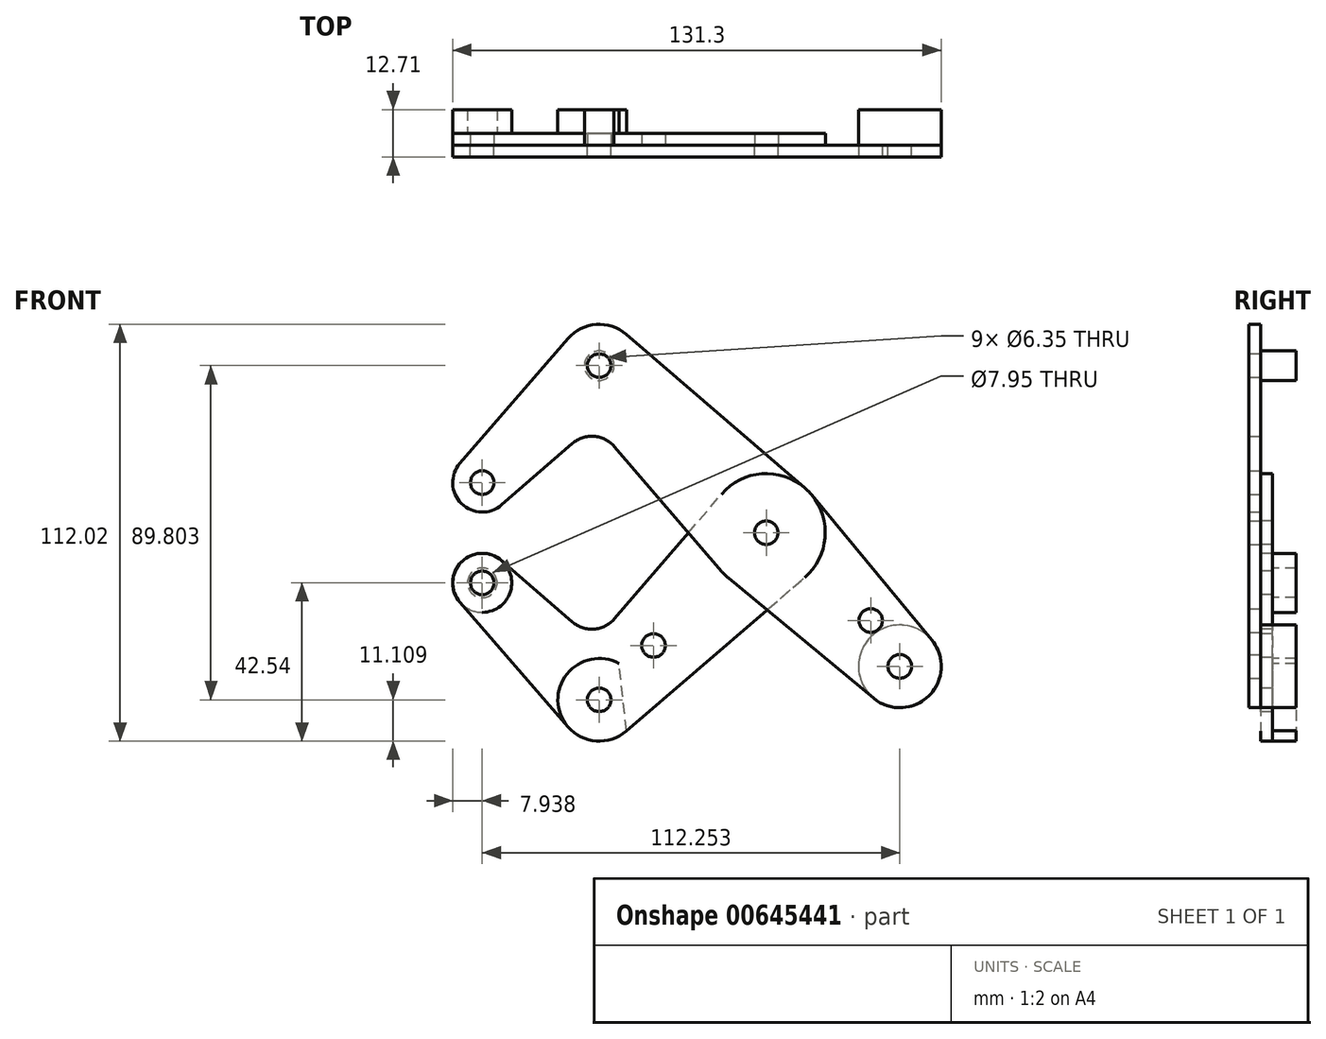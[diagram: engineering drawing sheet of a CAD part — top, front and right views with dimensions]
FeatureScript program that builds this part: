
annotation { "Feature Type Name" : "Feature", "Feature Type Description" : "" }
export const myFeature = defineFeature(function(context is Context, id is Id, definition is map)
    precondition{}
    {
        {
            var Q0;
            Q0=qCreatedBy(makeId("Front.planeOp"),FACE);
            var sketch = newSketch(context, id + "F0", { "sketchPlane" : qUnion([Q0])});
            skLineSegment(sketch, "E0", {"start": v(-76.33, 13.47) * mm, "end": v(-44.9, 44.9) * mm, "construction": true});
            skLineSegment(sketch, "E1", {"start": v(-44.9, 44.9) * mm, "end": v(35.92, -35.92) * mm, "construction": true});
            skCircle(sketch, "E2", {"center": v(-76.33, 13.47) * mm, "radius": 7.94 * mm});
            skCircle(sketch, "E3", {"center": v(-44.9, 44.9) * mm, "radius": 3.18 * mm});
            skCircle(sketch, "E4", {"center": v(-44.9, 44.9) * mm, "radius": 11.11 * mm});
            skCircle(sketch, "E5", {"center": v(0, 0) * mm, "radius": 15.88 * mm});
            skCircle(sketch, "E6", {"center": v(0, 0) * mm, "radius": 3.98 * mm});
            skCircle(sketch, "E7", {"center": v(35.92, -35.92) * mm, "radius": 11.11 * mm});
            skCircle(sketch, "E8", {"center": v(35.92, -35.92) * mm, "radius": 3.18 * mm});
            skCircle(sketch, "E9", {"center": v(-76.33, 13.47) * mm, "radius": 3.18 * mm});
            skCircle(sketch, "E10", {"center": v(0, 0) * mm, "radius": 3.18 * mm});
            skCircle(sketch, "E11", {"center": v(28.07, -23.58) * mm, "radius": 3.18 * mm});
            skLineSegment(sketch, "E12", {"start": v(-82.33, 18.67) * mm, "end": v(-53.3, 52.18) * mm});
            skLineSegment(sketch, "E13", {"start": v(-71.13, 7.47) * mm, "end": v(-52.08, 23.98) * mm});
            skLineSegment(sketch, "E14", {"start": v(-40.85, 23.15) * mm, "end": v(-12.04, -10.35) * mm});
            skLineSegment(sketch, "E15", {"start": v(-10.12, -12.23) * mm, "end": v(28.83, -44.48) * mm});
            skLineSegment(sketch, "E16", {"start": v(-37.66, 53.33) * mm, "end": v(10.35, 12.04) * mm});
            skLineSegment(sketch, "E17", {"start": v(12.23, 10.12) * mm, "end": v(44.48, -28.83) * mm});
            skLineSegment(sketch, "E18", {"start": v(0, 0) * mm, "end": v(11.23, 11.23) * mm, "construction": true});
            skArc(sketch, "E19.filletArc", {"start": v(-40.85, 23.15) * mm, "mid": v(-46.3, 25.9) * mm, "end": v(-52.08, 23.98) * mm});
            skLineSegment(sketch, "E20", {"start": v(0, 0) * mm, "end": v(-44.9, -44.9) * mm, "construction": true});
            skLineSegment(sketch, "E21", {"start": v(-44.9, -44.9) * mm, "end": v(-76.33, -13.47) * mm, "construction": true});
            skCircle(sketch, "E22", {"center": v(-76.33, -13.47) * mm, "radius": 7.94 * mm});
            skCircle(sketch, "E23", {"center": v(-76.33, -13.47) * mm, "radius": 3.18 * mm});
            skCircle(sketch, "E24", {"center": v(-44.9, -44.9) * mm, "radius": 11.11 * mm});
            skCircle(sketch, "E25", {"center": v(-30.3, -30.3) * mm, "radius": 3.18 * mm});
            skCircle(sketch, "E26", {"center": v(-44.9, -44.9) * mm, "radius": 3.18 * mm});
            skLineSegment(sketch, "E27", {"start": v(-82.33, -18.67) * mm, "end": v(-53.3, -52.18) * mm});
            skLineSegment(sketch, "E28", {"start": v(-71.13, -7.47) * mm, "end": v(-52.08, -23.98) * mm});
            skLineSegment(sketch, "E29", {"start": v(-40.85, -23.15) * mm, "end": v(-12.04, 10.35) * mm});
            skLineSegment(sketch, "E30", {"start": v(-37.66, -53.33) * mm, "end": v(10.35, -12.04) * mm});
            skArc(sketch, "E31.filletArc", {"start": v(-52.08, -23.98) * mm, "mid": v(-46.3, -25.9) * mm, "end": v(-40.85, -23.15) * mm});
            skSolve(sketch);
        }
        {
            var Q0;
            Q0=makeQuery(id+"F0.imprint","IMPRINT",FACE,{"disambiguationData":[TD([[makeQuery(id+"F0.imprint","IMPRINT",EDGE,{"derivedFrom":sQuery(id+"F0.wireOp",EDGE,"E9")}),-1.0]])]});
            var Q1;
            {var subQ0=sQuery(id+"F0.wireOp",EDGE,"E12");Q1=makeQuery(id+"F0.imprint","IMPRINT",FACE,{"disambiguationData":[TD([[makeQuery(id+"F0.imprint","IMPRINT",EDGE,{"derivedFrom":subQ0}),-1.0]])]});}
            var Q2;
            Q2=makeQuery(id+"F0.imprint","IMPRINT",FACE,{"disambiguationData":[TD([[makeQuery(id+"F0.imprint","IMPRINT",EDGE,{"derivedFrom":sQuery(id+"F0.wireOp",EDGE,"E3")}),-1.0]])]});
            var Q3;
            {var subQ0=sQuery(id+"F0.wireOp",EDGE,"E14");var subQ1=sQuery(id+"F0.wireOp",EDGE,"E5");var subQ2=makeQuery(id+"F0.imprint","INTERSECT",VERTEX,{"derivedFrom":[subQ1,subQ0]});Q3=makeQuery(id+"F0.imprint","IMPRINT",FACE,{"disambiguationData":[TD([[makeQuery(id+"F0.imprint","IMPRINT",EDGE,{"disambiguationData":[TD([[subQ2,1.0]])],"derivedFrom":subQ1}),-1.0]])]});}
            var Q4;
            Q4=makeQuery(id+"F0.imprint","IMPRINT",FACE,{"disambiguationData":[TD([[makeQuery(id+"F0.imprint","IMPRINT",EDGE,{"derivedFrom":sQuery(id+"F0.wireOp",EDGE,"E6")}),-1.0]])]});
            var Q5;
            Q5=makeQuery(id+"F0.imprint","IMPRINT",FACE,{"disambiguationData":[TD([[makeQuery(id+"F0.imprint","IMPRINT",EDGE,{"derivedFrom":sQuery(id+"F0.wireOp",EDGE,"E6")}),1.0]])]});
            var Q6;
            Q6=makeQuery(id+"F0.imprint","IMPRINT",FACE,{"disambiguationData":[TD([[makeQuery(id+"F0.imprint","IMPRINT",EDGE,{"derivedFrom":sQuery(id+"F0.wireOp",EDGE,"E11")}),-1.0]])]});
            var Q7;
            Q7=makeQuery(id+"F0.imprint","IMPRINT",FACE,{"disambiguationData":[TD([[makeQuery(id+"F0.imprint","IMPRINT",EDGE,{"derivedFrom":sQuery(id+"F0.wireOp",EDGE,"E8")}),-1.0]])]});
            var Q8;
            {var subQ0=sQuery(id+"F0.wireOp",EDGE,"E15");var subQ1=sQuery(id+"F0.wireOp",EDGE,"E5");var subQ2=makeQuery(id+"F0.imprint","INTERSECT",VERTEX,{"derivedFrom":[subQ1,subQ0]});Q8=makeQuery(id+"F0.imprint","IMPRINT",FACE,{"disambiguationData":[TD([[makeQuery(id+"F0.imprint","IMPRINT",EDGE,{"disambiguationData":[TD([[subQ2,-1.0]])],"derivedFrom":subQ1}),-1.0]])]});}
            extrude(context, id + "F1", {"entities" : qUnion([Q0, Q1, Q2, Q3, Q4, Q5, Q6, Q7, Q8]), "depth" : 3.17 * mm, "offsetDistance" : 25.4 * mm});
        }
        {
            var Q0;
            Q0=makeQuery(id+"F0.imprint","IMPRINT",FACE,{"disambiguationData":[TD([[makeQuery(id+"F0.imprint","IMPRINT",EDGE,{"derivedFrom":sQuery(id+"F0.wireOp",EDGE,"E23")}),-1.0]])]});
            var Q1;
            Q1=makeQuery(id+"F0.imprint","IMPRINT",FACE,{"disambiguationData":[TD([[makeQuery(id+"F0.imprint","IMPRINT",EDGE,{"derivedFrom":sQuery(id+"F0.wireOp",EDGE,"E25")}),-1.0]])]});
            var Q2;
            Q2=makeQuery(id+"F0.imprint","IMPRINT",FACE,{"disambiguationData":[TD([[makeQuery(id+"F0.imprint","IMPRINT",EDGE,{"derivedFrom":sQuery(id+"F0.wireOp",EDGE,"E26")}),-1.0]])]});
            var Q3;
            {var subQ0=sQuery(id+"F0.wireOp",EDGE,"E14");var subQ1=sQuery(id+"F0.wireOp",EDGE,"E5");var subQ2=makeQuery(id+"F0.imprint","INTERSECT",VERTEX,{"derivedFrom":[subQ1,subQ0]});Q3=makeQuery(id+"F0.imprint","IMPRINT",FACE,{"disambiguationData":[TD([[makeQuery(id+"F0.imprint","IMPRINT",EDGE,{"disambiguationData":[TD([[subQ2,1.0]])],"derivedFrom":subQ1}),-1.0]])]});}
            var Q4;
            {var subQ0=sQuery(id+"F0.wireOp",EDGE,"E15");var subQ1=sQuery(id+"F0.wireOp",EDGE,"E5");var subQ2=makeQuery(id+"F0.imprint","INTERSECT",VERTEX,{"derivedFrom":[subQ1,subQ0]});Q4=makeQuery(id+"F0.imprint","IMPRINT",FACE,{"disambiguationData":[TD([[makeQuery(id+"F0.imprint","IMPRINT",EDGE,{"disambiguationData":[TD([[subQ2,-1.0]])],"derivedFrom":subQ1}),-1.0]])]});}
            var Q5;
            Q5=makeQuery(id+"F0.imprint","IMPRINT",FACE,{"disambiguationData":[TD([[makeQuery(id+"F0.imprint","IMPRINT",EDGE,{"derivedFrom":sQuery(id+"F0.wireOp",EDGE,"E6")}),1.0]])]});
            var Q6;
            Q6=makeQuery(id+"F0.imprint","IMPRINT",FACE,{"disambiguationData":[TD([[makeQuery(id+"F0.imprint","IMPRINT",EDGE,{"derivedFrom":sQuery(id+"F0.wireOp",EDGE,"E6")}),-1.0]])]});
            var Q7;
            Q7=makeQuery(id+"F1.opExtrude","CAP_FACE",FACE,{"disambiguationData":[OSD([sQuery(id+"F0.wireOp",EDGE,"E2"),sQuery(id+"F0.wireOp",EDGE,"E3"),sQuery(id+"F0.wireOp",EDGE,"E4"),sQuery(id+"F0.wireOp",EDGE,"E5"),sQuery(id+"F0.wireOp",EDGE,"E7"),sQuery(id+"F0.wireOp",EDGE,"E8"),sQuery(id+"F0.wireOp",EDGE,"E9"),sQuery(id+"F0.wireOp",EDGE,"E10"),sQuery(id+"F0.wireOp",EDGE,"E11"),sQuery(id+"F0.wireOp",EDGE,"E12"),sQuery(id+"F0.wireOp",EDGE,"E13"),sQuery(id+"F0.wireOp",EDGE,"E14"),sQuery(id+"F0.wireOp",EDGE,"E15"),sQuery(id+"F0.wireOp",EDGE,"E16"),sQuery(id+"F0.wireOp",EDGE,"E17"),sQuery(id+"F0.wireOp",EDGE,"E19.filletArc"),sQuery(id+"F0.wireOp",EDGE,"E30")])],"isStart":false});
            extrude(context, id + "F2", {"entities" : qUnion([Q0, Q1, Q2, Q3, Q4, Q5, Q6, Q7]), "oppositeDirection" : true, "depth" : 3.17 * mm, "offsetDistance" : 25.4 * mm});
        }
        {
            var Q0;
            Q0=makeQuery(id+"F1.opExtrude","CAP_FACE",FACE,{"disambiguationData":[OSD([sQuery(id+"F0.wireOp",EDGE,"E2"),sQuery(id+"F0.wireOp",EDGE,"E3"),sQuery(id+"F0.wireOp",EDGE,"E4"),sQuery(id+"F0.wireOp",EDGE,"E5"),sQuery(id+"F0.wireOp",EDGE,"E7"),sQuery(id+"F0.wireOp",EDGE,"E8"),sQuery(id+"F0.wireOp",EDGE,"E9"),sQuery(id+"F0.wireOp",EDGE,"E10"),sQuery(id+"F0.wireOp",EDGE,"E11"),sQuery(id+"F0.wireOp",EDGE,"E12"),sQuery(id+"F0.wireOp",EDGE,"E13"),sQuery(id+"F0.wireOp",EDGE,"E14"),sQuery(id+"F0.wireOp",EDGE,"E15"),sQuery(id+"F0.wireOp",EDGE,"E16"),sQuery(id+"F0.wireOp",EDGE,"E17"),sQuery(id+"F0.wireOp",EDGE,"E19.filletArc")])],"isStart":false});
            var sketch = newSketch(context, id + "F3", { "sketchPlane" : qUnion([Q0])});
            skCircle(sketch, "E32", {"center": v(-44.9, 44.9) * mm, "radius": 3.98 * mm});
            skCircle(sketch, "E33.0", {"center": v(35.92, -35.92) * mm, "radius": 11.11 * mm});
            skSolve(sketch);
        }
        {
            var Q0;
            Q0=makeQuery(id+"F0.imprint","IMPRINT",FACE,{"disambiguationData":[TD([[makeQuery(id+"F0.imprint","IMPRINT",EDGE,{"derivedFrom":sQuery(id+"F0.wireOp",EDGE,"E25")}),-1.0]])]});
            var sketch = newSketch(context, id + "F4", { "sketchPlane" : qUnion([Q0])});
            skCircle(sketch, "E34.0", {"center": v(-76.33, -13.47) * mm, "radius": 7.94 * mm});
            skCircle(sketch, "E35", {"center": v(-76.33, -13.47) * mm, "radius": 3.98 * mm});
            skLineSegment(sketch, "E36.0", {"start": v(-71.13, -7.47) * mm, "end": v(-52.08, -23.98) * mm});
            skArc(sketch, "E37.0", {"start": v(-39.6, -35.14) * mm, "mid": v(-55.95, -46.13) * mm, "end": v(-37.58, -53.26) * mm});
            skLineSegment(sketch, "E38", {"start": v(-44.9, -44.9) * mm, "end": v(35.92, -35.92) * mm, "construction": true});
            skLineSegment(sketch, "E39", {"start": v(-39.6, -35.14) * mm, "end": v(-37.58, -53.26) * mm});
            skSolve(sketch);
        }
        {
            var Q0;
            Q0=qCreatedBy(makeId("Front.planeOp"),FACE);
            cPlane(context, id + "F5", {"entities" : qUnion([Q0]), "cplaneType" : CPlaneType.OFFSET, "offset" : 9.52 * mm, "oppositeDirection" : true, "width" : 152.4 * mm, "height" : 152.4 * mm});
        }
        {
            var Q0;
            Q0 = qSketchRegion(id + "F3", true);
            var Q1;
            Q1 = qSketchRegion(id + "F4", true);
            var Q2;
            Q2=qCreatedBy(id+"F5.planeOp",FACE);
            extrude(context, id + "F6", {"entities" : qUnion([Q0, Q1]), "endBound" : BoundingType.UP_TO_SURFACE, "oppositeDirection" : true, "depth" : 25.4 * mm, "endBoundEntityFace" : qUnion([Q2]), "offsetDistance" : 25.4 * mm});
        }
        {
            var Q0;
            Q0=makeQuery(id+"F2.opExtrude","SWEPT_BODY",BODY,{"disambiguationData":[OSD([sQuery(id+"F0.wireOp",EDGE,"E5"),sQuery(id+"F0.wireOp",EDGE,"E10"),sQuery(id+"F0.wireOp",EDGE,"E22"),sQuery(id+"F0.wireOp",EDGE,"E23"),sQuery(id+"F0.wireOp",EDGE,"E24"),sQuery(id+"F0.wireOp",EDGE,"E25"),sQuery(id+"F0.wireOp",EDGE,"E26"),sQuery(id+"F0.wireOp",EDGE,"E27"),sQuery(id+"F0.wireOp",EDGE,"E28"),sQuery(id+"F0.wireOp",EDGE,"E29"),sQuery(id+"F0.wireOp",EDGE,"E30"),sQuery(id+"F0.wireOp",EDGE,"E31.filletArc")])]});
            var Q1;
            Q1=makeQuery(id+"F1.opExtrude","SWEPT_BODY",BODY,{"disambiguationData":[OSD([sQuery(id+"F0.wireOp",EDGE,"E2"),sQuery(id+"F0.wireOp",EDGE,"E3"),sQuery(id+"F0.wireOp",EDGE,"E4"),sQuery(id+"F0.wireOp",EDGE,"E5"),sQuery(id+"F0.wireOp",EDGE,"E7"),sQuery(id+"F0.wireOp",EDGE,"E8"),sQuery(id+"F0.wireOp",EDGE,"E9"),sQuery(id+"F0.wireOp",EDGE,"E10"),sQuery(id+"F0.wireOp",EDGE,"E11"),sQuery(id+"F0.wireOp",EDGE,"E12"),sQuery(id+"F0.wireOp",EDGE,"E13"),sQuery(id+"F0.wireOp",EDGE,"E14"),sQuery(id+"F0.wireOp",EDGE,"E15"),sQuery(id+"F0.wireOp",EDGE,"E16"),sQuery(id+"F0.wireOp",EDGE,"E17"),sQuery(id+"F0.wireOp",EDGE,"E19.filletArc")])]});
            var Q2;
            Q2=makeQuery(id+"F2.opExtrude","SWEPT_BODY",BODY,{"disambiguationData":[OSD([sQuery(id+"F0.wireOp",EDGE,"E2"),sQuery(id+"F0.wireOp",EDGE,"E3"),sQuery(id+"F0.wireOp",EDGE,"E4"),sQuery(id+"F0.wireOp",EDGE,"E5"),sQuery(id+"F0.wireOp",EDGE,"E7"),sQuery(id+"F0.wireOp",EDGE,"E8"),sQuery(id+"F0.wireOp",EDGE,"E9"),sQuery(id+"F0.wireOp",EDGE,"E10"),sQuery(id+"F0.wireOp",EDGE,"E11"),sQuery(id+"F0.wireOp",EDGE,"E12"),sQuery(id+"F0.wireOp",EDGE,"E13"),sQuery(id+"F0.wireOp",EDGE,"E14"),sQuery(id+"F0.wireOp",EDGE,"E15"),sQuery(id+"F0.wireOp",EDGE,"E16"),sQuery(id+"F0.wireOp",EDGE,"E17"),sQuery(id+"F0.wireOp",EDGE,"E19.filletArc")])]});
            var Q3;
            Q3=makeQuery(id+"F6.opExtrude","SWEPT_BODY",BODY,{"disambiguationData":[OSD([sQuery(id+"F3.wireOp",EDGE,"E32")])]});
            var Q4;
            Q4=makeQuery(id+"F6.opExtrude","SWEPT_BODY",BODY,{"disambiguationData":[OSD([sQuery(id+"F3.wireOp",EDGE,"E33.0")])]});
            var Q5;
            Q5=makeQuery(id+"F6.opExtrude","SWEPT_BODY",BODY,{"disambiguationData":[OSD([sQuery(id+"F4.wireOp",EDGE,"E34.0"),sQuery(id+"F4.wireOp",EDGE,"E35")])]});
            var Q6;
            Q6=makeQuery(id+"F6.opExtrude","SWEPT_BODY",BODY,{"disambiguationData":[OSD([sQuery(id+"F4.wireOp",EDGE,"E37.0"),sQuery(id+"F4.wireOp",EDGE,"E39")])]});
            booleanBodies(context, id + "F7", {"operationType" : BooleanOperationType.SUBTRACTION, "tools" : qUnion([Q0, Q1]), "targets" : qUnion([Q2, Q3, Q4, Q5, Q6]), "keepTools" : true});
        }
    });
